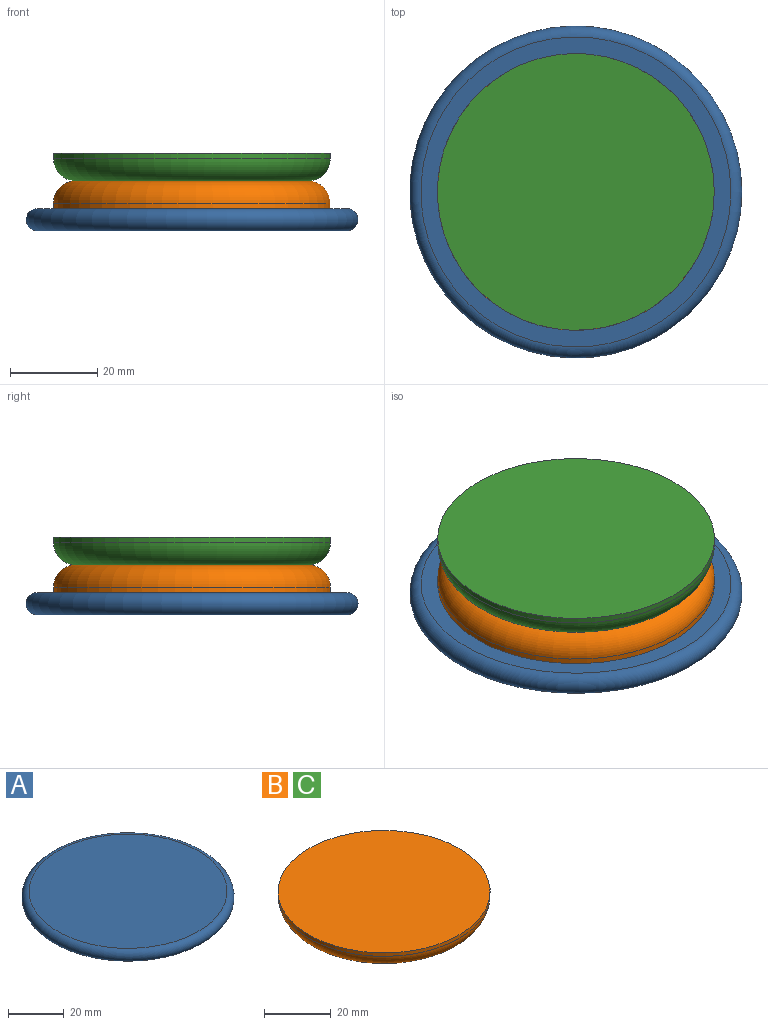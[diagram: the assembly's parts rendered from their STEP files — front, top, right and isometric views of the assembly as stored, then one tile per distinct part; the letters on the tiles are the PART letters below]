
ASSEMBLY  parts=3 mates=4
PART A: 3 faces, bbox 82.5x82.5x5.1 mm
  f0: plane 71.12x71.12mm, normal (0,0,1), area 3972.6mm2, adj f2
  f1: plane 71.12x71.12mm, normal (0,0,-1), area 3972.6mm2, adj f2
  f2: torus R=35.56mm, axis (0,0,1), area 1864mm2, adj f0,f1
PART B: 4 faces, bbox 68.7x68.7x8.7 mm
  f0: cylinder r=31.75mm len=63.5mm, axis (0,0,-1), area 253.4mm2, adj f1,f3
  f1: plane 63.5x63.5mm, normal (0,0,1), area 3166.9mm2, adj f0
  f2: plane 53.34x53.34mm, normal (0,0,-1), area 2234.6mm2, adj f3
  f3: torus R=26.67mm, axis (0,0,1), area 1499.3mm2, adj f0,f2
PART C: same geometry as B
PLACE A t=(59.9,-85.51,31.46)mm
PLACE B rot(axis=(0,1,0),180deg) t=(-67.23,-99.86,42.89)mm
PLACE C t=(68.18,-99.86,42.89)mm
MATE planar B.f0 <-> C.f0  axis (0,0,1) through (0.48,-69.06,42.89)mm
MATE fastened C.f0 <-> B.f0  axis (0,0,-1) through (0.48,-69.06,42.89)mm
MATE planar A.f2 <-> B.f0  axis (0,0,1) through (0.48,-69.06,36.54)mm
MATE fastened A.f2 <-> B.f0  axis (0,0,1) through (0.48,-69.06,36.54)mm
